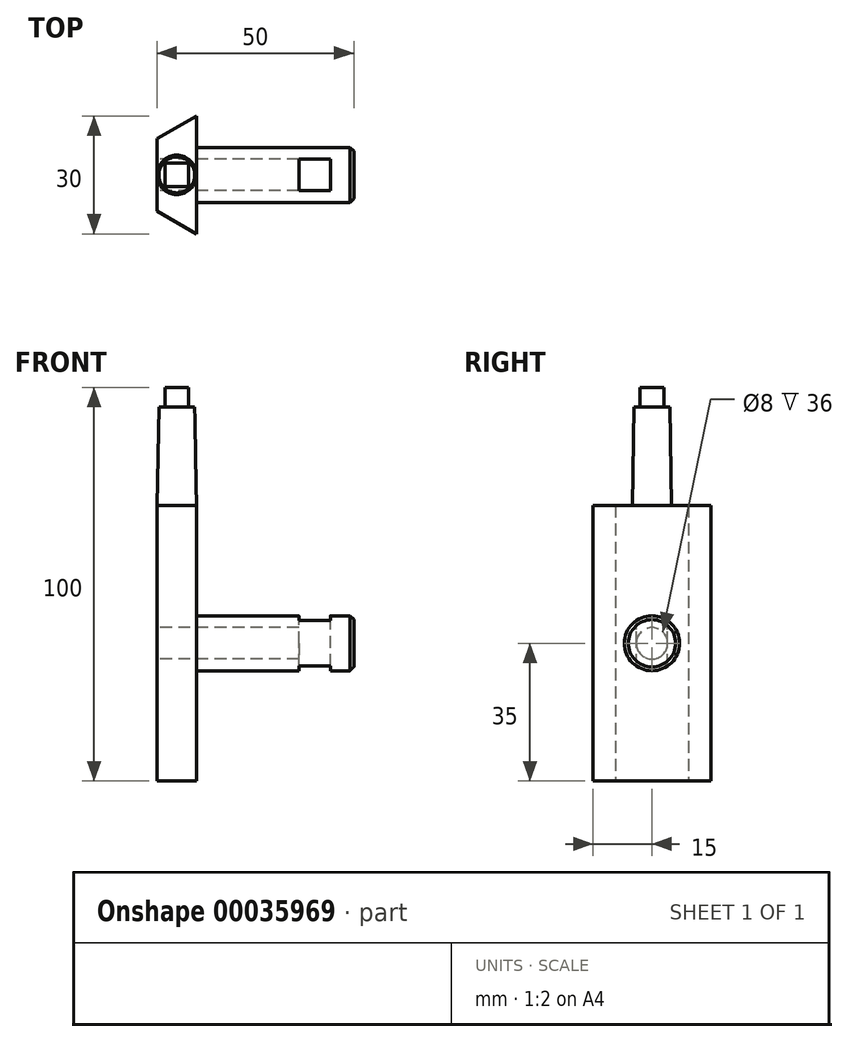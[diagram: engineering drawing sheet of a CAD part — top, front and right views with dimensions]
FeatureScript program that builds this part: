
annotation { "Feature Type Name" : "Feature", "Feature Type Description" : "" }
export const myFeature = defineFeature(function(context is Context, id is Id, definition is map)
    precondition{}
    {
        {
            var Q0;
            Q0=qCreatedBy(makeId("Top.planeOp"),FACE);
            var sketch = newSketch(context, id + "F0", { "sketchPlane" : qUnion([Q0])});
            skLineSegment(sketch, "E0", {"start": v(0, 0) * mm, "end": v(0, 15) * mm});
            skLineSegment(sketch, "E1", {"start": v(0, 15) * mm, "end": v(-10, 9.23) * mm});
            skLineSegment(sketch, "E2.MirrorCS", {"start": v(0, -15) * mm, "end": v(-10, -9.23) * mm});
            skLineSegment(sketch, "E3.MirrorCS", {"start": v(0, 0) * mm, "end": v(0, -15) * mm});
            skLineSegment(sketch, "E4", {"start": v(-10, 9.23) * mm, "end": v(-10, -9.23) * mm});
            skPoint(sketch, "E5.orphan", {"position": v(-25.98, 0) * mm});
            skSolve(sketch);
        }
        {
            var Q0;
            Q0=makeQuery(id+"F0.imprint","IMPRINT",FACE,{"disambiguationData":[TD([[makeQuery(id+"F0.imprint","IMPRINT",EDGE,{"derivedFrom":sQuery(id+"F0.wireOp",EDGE,"E0")}),1.0]])]});
            extrude(context, id + "F1", {"entities" : qUnion([Q0]), "depth" : 70 * mm});
        }
        {
            var Q0;
            Q0=qCreatedBy(makeId("Right.planeOp"),FACE);
            var sketch = newSketch(context, id + "F2", { "sketchPlane" : qUnion([Q0])});
            skLineSegment(sketch, "E6", {"start": v(0, 0) * mm, "end": v(0, 35) * mm});
            skCircle(sketch, "E7", {"center": v(0, 35) * mm, "radius": 7 * mm});
            skCircle(sketch, "E8", {"center": v(0, 35) * mm, "radius": 4 * mm});
            skSolve(sketch);
        }
        {
            var Q0;
            Q0=makeQuery(id+"F2.imprint","IMPRINT",FACE,{"disambiguationData":[TD([[makeQuery(id+"F2.imprint","IMPRINT",EDGE,{"derivedFrom":sQuery(id+"F2.wireOp",EDGE,"E7")}),1.0]])]});
            var Q1;
            Q1=makeQuery(id+"F2.imprint","IMPRINT",FACE,{"disambiguationData":[TD([[makeQuery(id+"F2.imprint","IMPRINT",EDGE,{"derivedFrom":sQuery(id+"F2.wireOp",EDGE,"E8")}),1.0]])]});
            extrude(context, id + "F3", {"entities" : qUnion([Q0, Q1]), "operationType" : NewBodyOperationType.ADD, "depth" : 40 * mm});
        }
        {
            var Q0;
            Q0=makeQuery(id+"F3.opExtrude","CAP_EDGE",EDGE,{"disambiguationData":[OSD([sQuery(id+"F2.wireOp",EDGE,"E7")])],"isStart":false});
            chamfer(context, id + "F4", {"entities" : qUnion([Q0]), "width" : 1 * mm, "tangentPropagation" : true});
        }
        {
            var Q0;
            Q0=qCreatedBy(makeId("Top.planeOp"),FACE);
            var sketch = newSketch(context, id + "F5", { "sketchPlane" : qUnion([Q0])});
            skLineSegment(sketch, "E9", {"start": v(0, 0) * mm, "end": v(26, 0) * mm});
            skLineSegment(sketch, "E10.bottom", {"start": v(34, -4) * mm, "end": v(26, -4) * mm});
            skLineSegment(sketch, "E10.top", {"start": v(34, 4) * mm, "end": v(26, 4) * mm});
            skLineSegment(sketch, "E10.left", {"start": v(34, -4) * mm, "end": v(34, 4) * mm});
            skLineSegment(sketch, "E10.right", {"start": v(26, -4) * mm, "end": v(26, 4) * mm});
            skPoint(sketch, "E10.middle", {"position": v(30, 0) * mm});
            skSolve(sketch);
        }
        {
            var Q0;
            Q0 = qSketchRegion(id + "F5", true);
            extrude(context, id + "F6", {"entities" : qUnion([Q0]), "operationType" : NewBodyOperationType.REMOVE, "oppositeDirection" : true, "depth" : 25 * mm, "hasSecondDirection" : true, "secondDirectionOppositeDirection" : false, "secondDirectionDepth" : 100 * mm});
        }
        {
            var Q0;
            Q0=qCreatedBy(makeId("Right.planeOp"),FACE);
            var sketch = newSketch(context, id + "F7", { "sketchPlane" : qUnion([Q0])});
            skCircle(sketch, "E11", {"center": v(0, 35) * mm, "radius": 4 * mm});
            skSolve(sketch);
        }
        {
            var Q0;
            Q0 = qSketchRegion(id + "F7", true);
            extrude(context, id + "F8", {"entities" : qUnion([Q0]), "operationType" : NewBodyOperationType.REMOVE, "depth" : 30 * mm, "hasSecondDirection" : true, "secondDirectionOppositeDirection" : true, "secondDirectionDepth" : 25 * mm});
        }
        {
            var Q0;
            Q0=qCreatedBy(makeId("Top.planeOp"),FACE);
            cPlane(context, id + "F9", {"entities" : qUnion([Q0]), "cplaneType" : CPlaneType.OFFSET, "offset" : 70 * mm, "width" : 150 * mm, "height" : 150 * mm});
        }
        {
            var Q0;
            Q0=qCreatedBy(id+"F9.planeOp",FACE);
            var sketch = newSketch(context, id + "F10", { "sketchPlane" : qUnion([Q0])});
            skLineSegment(sketch, "E12", {"start": v(0, 0) * mm, "end": v(-5, 0) * mm});
            skCircle(sketch, "E13", {"center": v(-5, 0) * mm, "radius": 5 * mm});
            skSolve(sketch);
        }
        {
            var Q0;
            Q0 = qSketchRegion(id + "F10", true);
            extrude(context, id + "F11", {"entities" : qUnion([Q0]), "operationType" : NewBodyOperationType.ADD, "depth" : 30 * mm, "hasDraft" : true, "draftAngle" : 1 * degree, "draftPullDirection" : true});
        }
        {
            var Q0;
            Q0=qCreatedBy(id+"F9.planeOp",FACE);
            var sketch = newSketch(context, id + "F12", { "sketchPlane" : qUnion([Q0])});
            skLineSegment(sketch, "E14", {"start": v(0, 0) * mm, "end": v(-5, 0) * mm});
            skLineSegment(sketch, "E15.bottom", {"start": v(-8, -3) * mm, "end": v(-2, -3) * mm});
            skLineSegment(sketch, "E15.top", {"start": v(-8, 3) * mm, "end": v(-2, 3) * mm});
            skLineSegment(sketch, "E15.left", {"start": v(-8, -3) * mm, "end": v(-8, 3) * mm});
            skLineSegment(sketch, "E15.right", {"start": v(-2, -3) * mm, "end": v(-2, 3) * mm});
            skPoint(sketch, "E15.middle", {"position": v(-5, 0) * mm});
            skCircle(sketch, "E16", {"center": v(-5, 0) * mm, "radius": 21.01 * mm});
            skSolve(sketch);
        }
        {
            var Q0;
            Q0 = qSketchRegion(id + "F12", true);
            extrude(context, id + "F13", {"entities" : qUnion([Q0]), "operationType" : NewBodyOperationType.REMOVE, "depth" : 40 * mm, "hasSecondDirection" : true, "secondDirectionOppositeDirection" : false, "secondDirectionDepth" : 25 * mm});
        }
    });
